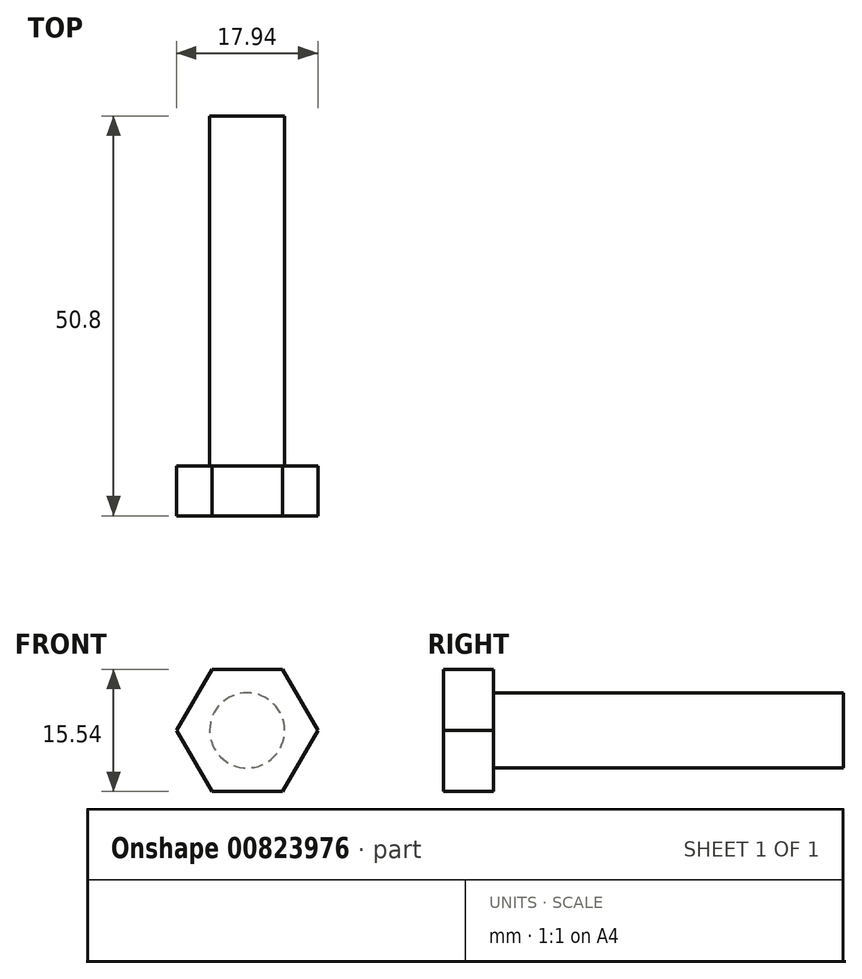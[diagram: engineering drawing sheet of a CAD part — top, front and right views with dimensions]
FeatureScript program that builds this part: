
annotation { "Feature Type Name" : "Feature", "Feature Type Description" : "" }
export const myFeature = defineFeature(function(context is Context, id is Id, definition is map)
    precondition{}
    {
        {
            var Q0;
            Q0=qCreatedBy(makeId("Front.planeOp"),FACE);
            var sketch = newSketch(context, id + "F0", { "sketchPlane" : qUnion([Q0])});
            skCircle(sketch, "E0", {"center": v(0, 0) * mm, "radius": 4.76 * mm});
            skSolve(sketch);
        }
        {
            var Q0;
            Q0=makeQuery(id+"F0.imprint","IMPRINT",FACE,{"disambiguationData":[TD([[makeQuery(id+"F0.imprint","IMPRINT",EDGE,{"derivedFrom":sQuery(id+"F0.wireOp",EDGE,"E0")}),1.0]])]});
            extrude(context, id + "F1", {"entities" : qUnion([Q0]), "endBound" : BoundingType.SYMMETRIC, "depth" : 44.45 * mm, "offsetDistance" : 25.4 * mm});
        }
        {
            var Q0;
            Q0=makeQuery(id+"F1.opExtrude","CAP_FACE",FACE,{"disambiguationData":[OSD([sQuery(id+"F0.wireOp",EDGE,"E0")])],"isStart":false});
            var sketch = newSketch(context, id + "F2", { "sketchPlane" : qUnion([Q0])});
            skCircle(sketch, "E1.cCircle", {"center": v(0, 0) * mm, "radius": 7.77 * mm, "construction": true});
            skLineSegment(sketch, "E1.0", {"start": v(4.49, -7.77) * mm, "end": v(-4.49, -7.77) * mm});
            skLineSegment(sketch, "E1.1", {"start": v(-4.49, -7.77) * mm, "end": v(-8.97, 0) * mm});
            skLineSegment(sketch, "E1.2", {"start": v(-8.97, 0) * mm, "end": v(-4.49, 7.77) * mm});
            skLineSegment(sketch, "E1.3", {"start": v(-4.49, 7.77) * mm, "end": v(4.49, 7.77) * mm});
            skLineSegment(sketch, "E1.4", {"start": v(4.49, 7.77) * mm, "end": v(8.97, 0) * mm});
            skLineSegment(sketch, "E1.5", {"start": v(8.97, 0) * mm, "end": v(4.49, -7.77) * mm});
            skPoint(sketch, "E1.0.midPoint", {"position": v(0, -7.77) * mm});
            skSolve(sketch);
        }
        {
            var Q0;
            Q0=makeQuery(id+"F2.imprint","IMPRINT",FACE,{"disambiguationData":[TD([[makeQuery(id+"F2.imprint","IMPRINT",EDGE,{"derivedFrom":sQuery(id+"F2.wireOp",EDGE,"E1.0")}),-1.0]])]});
            var Q1;
            Q1=makeQuery(id+"F2.imprint","IMPRINT",FACE,{"disambiguationData":[TD([[makeQuery(id+"F2.imprint","IMPRINT",EDGE,{"derivedFrom":makeQuery(id+"F1.opExtrude","CAP_EDGE",EDGE,{"disambiguationData":[OSD([sQuery(id+"F0.wireOp",EDGE,"E0")])],"isStart":false})}),1.0]])]});
            extrude(context, id + "F3", {"entities" : qUnion([Q0, Q1]), "operationType" : NewBodyOperationType.ADD, "depth" : 6.35 * mm, "offsetDistance" : 25.4 * mm});
        }
    });
